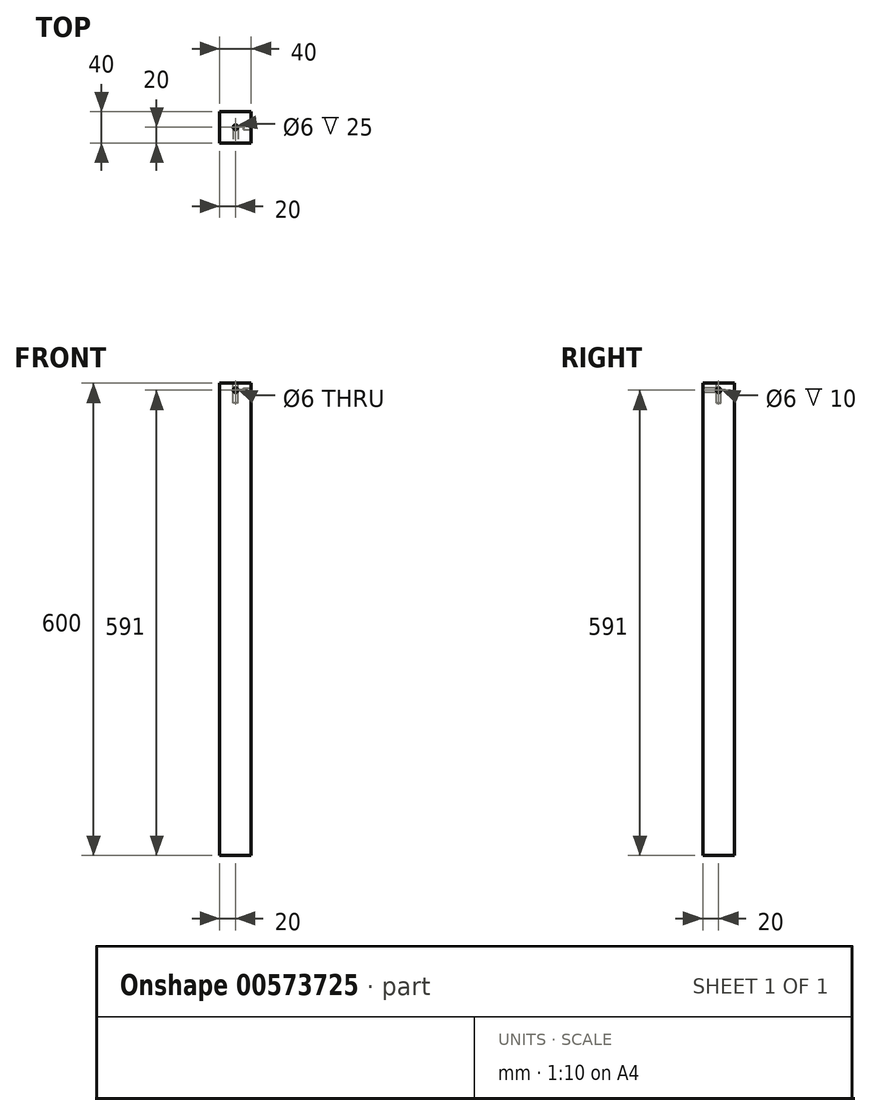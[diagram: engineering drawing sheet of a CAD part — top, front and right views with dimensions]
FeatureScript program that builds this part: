
annotation { "Feature Type Name" : "Feature", "Feature Type Description" : "" }
export const myFeature = defineFeature(function(context is Context, id is Id, definition is map)
    precondition{}
    {
        {
            var Q0;
            Q0=qCreatedBy(makeId("Top.planeOp"),FACE);
            var sketch = newSketch(context, id + "F0", { "sketchPlane" : qUnion([Q0])});
            skLineSegment(sketch, "E0.bottom", {"start": v(0, 0) * mm, "end": v(40, 0) * mm});
            skLineSegment(sketch, "E0.top", {"start": v(0, 40) * mm, "end": v(40, 40) * mm});
            skLineSegment(sketch, "E0.left", {"start": v(0, 0) * mm, "end": v(0, 40) * mm});
            skLineSegment(sketch, "E0.right", {"start": v(40, 0) * mm, "end": v(40, 40) * mm});
            skSolve(sketch);
        }
        {
            var Q0;
            Q0=makeQuery(id+"F0.imprint","IMPRINT",FACE,{"disambiguationData":[TD([[makeQuery(id+"F0.imprint","IMPRINT",EDGE,{"derivedFrom":sQuery(id+"F0.wireOp",EDGE,"E0.bottom")}),1.0]])]});
            extrude(context, id + "F1", {"entities" : qUnion([Q0]), "depth" : 600 * mm, "offsetDistance" : 25 * mm});
        }
        {
            var Q0;
            Q0=makeQuery(id+"F1.opExtrude","CAP_FACE",FACE,{"disambiguationData":[OSD([sQuery(id+"F0.wireOp",EDGE,"E0.bottom"),sQuery(id+"F0.wireOp",EDGE,"E0.top"),sQuery(id+"F0.wireOp",EDGE,"E0.left"),sQuery(id+"F0.wireOp",EDGE,"E0.right")])],"isStart":false});
            var sketch = newSketch(context, id + "F2", { "sketchPlane" : qUnion([Q0])});
            skCircle(sketch, "E1", {"center": v(20, 20) * mm, "radius": 3 * mm});
            skPoint(sketch, "E2", {"position": v(20, 40) * mm});
            skPoint(sketch, "E3", {"position": v(0, 20) * mm});
            skSolve(sketch);
        }
        {
            var Q0;
            Q0=qSketchRegion(id+"F2",true);
            extrude(context, id + "F3", {"entities" : qUnion([Q0]), "operationType" : NewBodyOperationType.REMOVE, "oppositeDirection" : true, "depth" : 25 * mm, "offsetDistance" : 25 * mm});
        }
        {
            var Q0;
            Q0=makeQuery(id+"F1.opExtrude","SWEPT_FACE",FACE,{"disambiguationData":[OSD([sQuery(id+"F0.wireOp",EDGE,"E0.bottom")])]});
            var sketch = newSketch(context, id + "F4", { "sketchPlane" : qUnion([Q0])});
            skCircle(sketch, "E4", {"center": v(20, 591) * mm, "radius": 3 * mm});
            skSolve(sketch);
        }
        {
            var Q0;
            Q0 = qSketchRegion(id + "F4", true);
            extrude(context, id + "F5", {"entities" : qUnion([Q0]), "operationType" : NewBodyOperationType.REMOVE, "oppositeDirection" : true, "depth" : 20 * mm, "offsetDistance" : 25 * mm});
        }
        {
            var Q0;
            Q0=makeQuery(id+"F1.opExtrude","SWEPT_FACE",FACE,{"disambiguationData":[OSD([sQuery(id+"F0.wireOp",EDGE,"E0.right")])]});
            var sketch = newSketch(context, id + "F6", { "sketchPlane" : qUnion([Q0])});
            skCircle(sketch, "E5", {"center": v(20, 591) * mm, "radius": 3 * mm});
            skSolve(sketch);
        }
        {
            var Q0;
            Q0 = qSketchRegion(id + "F6", true);
            extrude(context, id + "F7", {"entities" : qUnion([Q0]), "operationType" : NewBodyOperationType.REMOVE, "oppositeDirection" : true, "depth" : 10 * mm, "offsetDistance" : 25 * mm});
        }
    });
